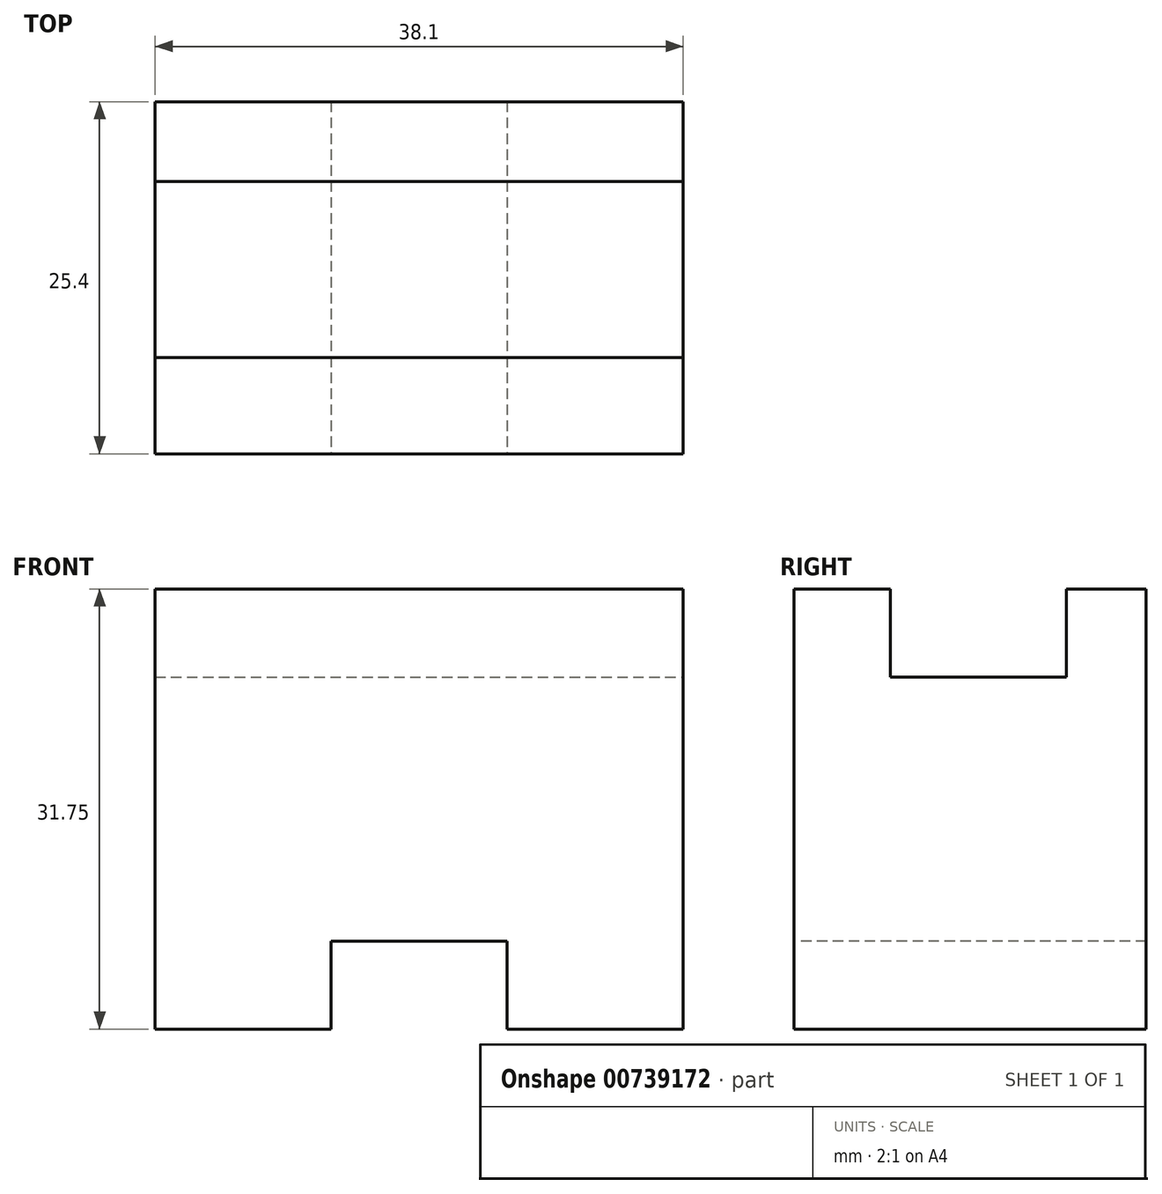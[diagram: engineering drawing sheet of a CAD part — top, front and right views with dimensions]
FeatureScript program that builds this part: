
annotation { "Feature Type Name" : "Feature", "Feature Type Description" : "" }
export const myFeature = defineFeature(function(context is Context, id is Id, definition is map)
    precondition{}
    {
        {
            var Q0;
            Q0=qCreatedBy(makeId("Front.planeOp"),FACE);
            var sketch = newSketch(context, id + "F0", { "sketchPlane" : qUnion([Q0])});
            skLineSegment(sketch, "E0", {"start": v(0, 31.75) * mm, "end": v(0, 0) * mm});
            skLineSegment(sketch, "E1", {"start": v(0, 0) * mm, "end": v(38.1, 0) * mm});
            skLineSegment(sketch, "E2", {"start": v(38.1, 0) * mm, "end": v(38.1, 31.75) * mm});
            skLineSegment(sketch, "E3", {"start": v(38.1, 31.75) * mm, "end": v(0, 31.75) * mm});
            skSolve(sketch);
        }
        {
            var Q0;
            Q0=makeQuery(id+"F0.imprint","IMPRINT",FACE,{"disambiguationData":[TD([[makeQuery(id+"F0.imprint","IMPRINT",EDGE,{"derivedFrom":sQuery(id+"F0.wireOp",EDGE,"E0")}),1.0]])]});
            extrude(context, id + "F1", {"entities" : qUnion([Q0]), "depth" : 25.4 * mm, "offsetDistance" : 25.4 * mm});
        }
        {
            var Q0;
            Q0=makeQuery(id+"F1.opExtrude","CAP_FACE",FACE,{"disambiguationData":[OSD([sQuery(id+"F0.wireOp",EDGE,"E0"),sQuery(id+"F0.wireOp",EDGE,"E1"),sQuery(id+"F0.wireOp",EDGE,"E2"),sQuery(id+"F0.wireOp",EDGE,"E3")])],"isStart":false});
            var sketch = newSketch(context, id + "F2", { "sketchPlane" : qUnion([Q0])});
            skLineSegment(sketch, "E4", {"start": v(12.7, 0) * mm, "end": v(12.7, 6.35) * mm});
            skLineSegment(sketch, "E5", {"start": v(12.7, 6.35) * mm, "end": v(25.4, 6.35) * mm});
            skLineSegment(sketch, "E6", {"start": v(25.4, 6.35) * mm, "end": v(25.4, 0) * mm});
            skSolve(sketch);
        }
        {
            var Q0;
            {var subQ0=sQuery(id+"F2.wireOp",EDGE,"E4");Q0=makeQuery(id+"F2.imprint","IMPRINT",FACE,{"disambiguationData":[TD([[makeQuery(id+"F2.imprint","IMPRINT",EDGE,{"derivedFrom":subQ0}),-1.0]])]});}
            extrude(context, id + "F3", {"entities" : qUnion([Q0]), "operationType" : NewBodyOperationType.REMOVE, "endBound" : BoundingType.THROUGH_ALL, "oppositeDirection" : true, "depth" : 25.4 * mm, "offsetDistance" : 25.4 * mm});
        }
        {
            var Q0;
            Q0=makeQuery(id+"F1.opExtrude","SWEPT_FACE",FACE,{"disambiguationData":[OSD([sQuery(id+"F0.wireOp",EDGE,"E2")])]});
            var sketch = newSketch(context, id + "F4", { "sketchPlane" : qUnion([Q0])});
            skLineSegment(sketch, "E7", {"start": v(-18.45, 31.75) * mm, "end": v(-18.45, 25.4) * mm});
            skLineSegment(sketch, "E8", {"start": v(-18.45, 25.4) * mm, "end": v(-5.75, 25.4) * mm});
            skLineSegment(sketch, "E9", {"start": v(-5.75, 25.4) * mm, "end": v(-5.75, 31.75) * mm});
            skSolve(sketch);
        }
        {
            var Q0;
            Q0 = qSketchRegion(id + "F4", true);
            var Q1;
            {var subQ0=sQuery(id+"F4.wireOp",EDGE,"E7");Q1=makeQuery(id+"F4.imprint","IMPRINT",FACE,{"disambiguationData":[TD([[makeQuery(id+"F4.imprint","IMPRINT",EDGE,{"derivedFrom":subQ0}),1.0]])]});}
            extrude(context, id + "F5", {"entities" : qUnion([Q0, Q1]), "operationType" : NewBodyOperationType.REMOVE, "endBound" : BoundingType.THROUGH_ALL, "oppositeDirection" : true, "depth" : 25.4 * mm, "offsetDistance" : 25.4 * mm});
        }
    });
